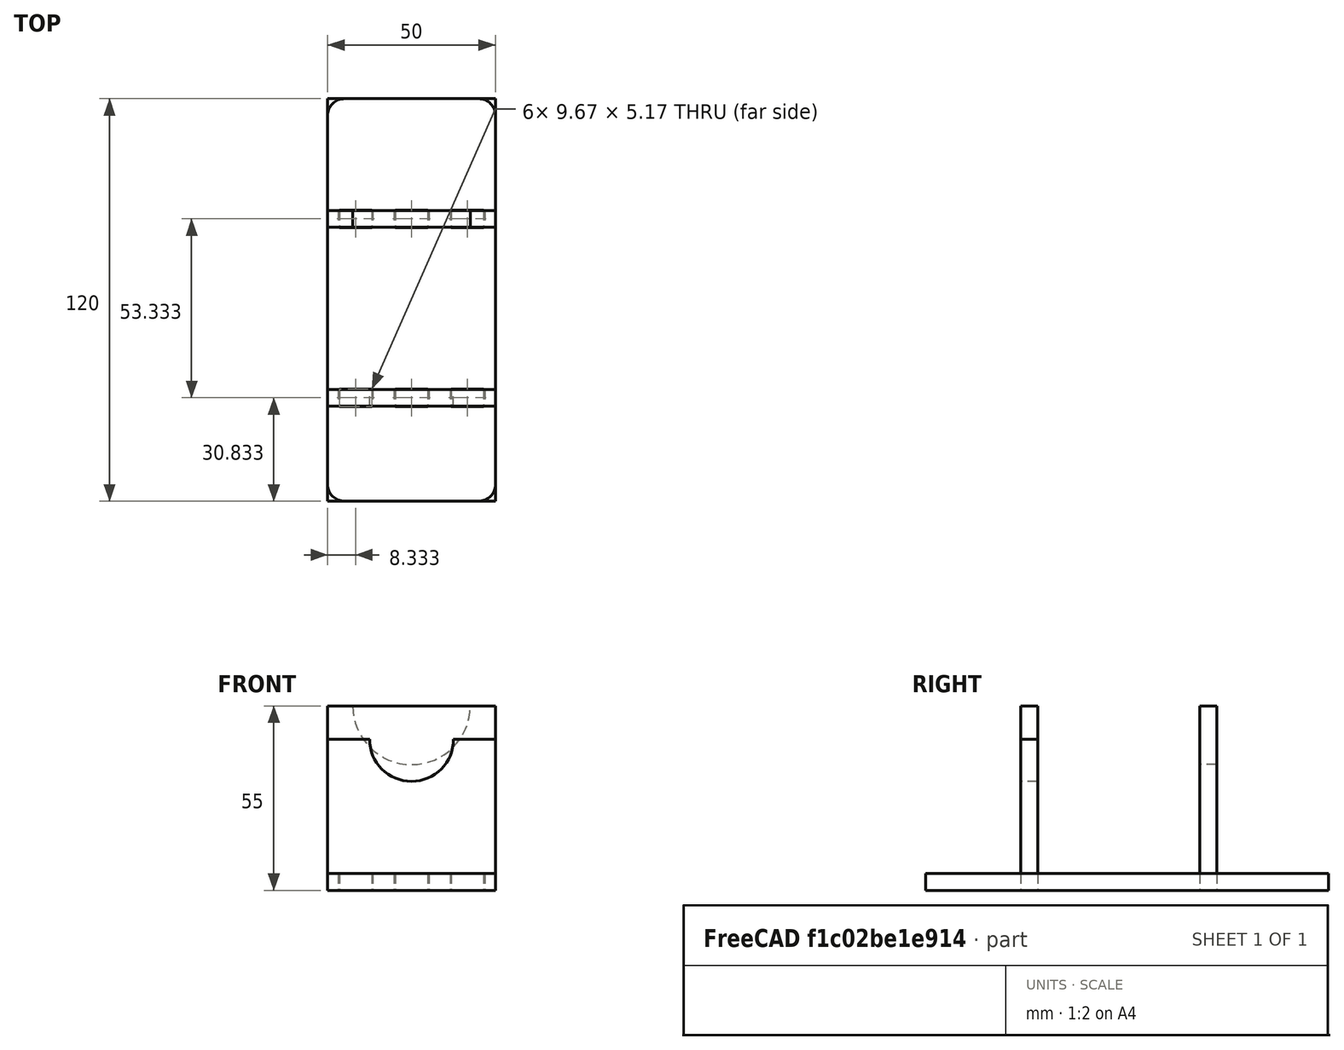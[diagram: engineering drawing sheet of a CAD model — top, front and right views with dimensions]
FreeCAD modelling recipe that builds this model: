
FCSTD DOCUMENT  (FreeCAD 0.19R24276 (Git))
Label: soldering_iron_stand
License: All rights reserved
LicenseURL: http://en.wikipedia.org/wiki/All_rights_reserved
objects: TechDraw::DrawProjGroupItem×27, TechDraw::DrawViewDimension×14, Part::Feature×6, PartDesign::FeatureBase×3, PartDesign::Body×3, TechDraw::DrawSVGTemplate×3, TechDraw::DrawProjGroup×3, TechDraw::DrawPage×3, Part::FeaturePython×2, Sketcher::SketchObject×2, PartDesign::Pocket×2, Spreadsheet::Sheet×1, App::DocumentObjectGroup×1, PartDesign::Fillet×1
note: 22 computed .brp shape members not serialized (recipe doc carries the construction recipe); baked Part::Feature solids carry a one-line shape summary decoded from their .brp

FEATURE [Spreadsheet::Sheet] Spreadsheet  label="parameters"
  cells = A1=width; B1(width)=120; A2=height; B2(height)=60; A3=depth; B3(depth)=50; A4=thickness; B4(thickness)=5
FEATURE [Part::Feature] face_panel
  Placement = pos=(0,-33.3333,0) rot=(0,0,1;0rad)
  shape: bbox 50 x 5 x 50 mm, 6 faces (baked)
  expr: .Placement.Base.y = <<parameters>>.depth / 1.5 * -1
FEATURE [Part::Feature] behind_panel
  Placement = pos=(0,-86.6667,0) rot=(0,0,1;0rad)
  shape: bbox 50 x 5 x 50 mm, 6 faces (baked)
  expr: .Placement.Base.y = (<<parameters>>.width - <<parameters>>.depth / 1.5) * -1
FEATURE [Part::Feature] bottom_panel
  shape: bbox 50 x 120 x 5 mm, 6 faces (baked)
FEATURE [Part::FeaturePython] Box  # WARN: FeaturePython — macro-defined, semantics opaque (R4)
  parts = -> [face_panel,behind_panel,bottom_panel]
FEATURE [App::DocumentObjectGroup] MultiJoin_origin_parts
  Group = -> [face_panel,behind_panel,bottom_panel]
FEATURE [Part::Feature] face_panel_tab
  shape: bbox 50 x 5 x 55 mm, 24 faces (baked)
FEATURE [Part::Feature] behind_panel_tab
  shape: bbox 50 x 5 x 55 mm, 24 faces (baked)
FEATURE [Part::Feature] bottom_panel_tab
  shape: bbox 50 x 120 x 5 mm, 30 faces (baked)
FEATURE [Part::FeaturePython] MultiJoin  # WARN: FeaturePython — macro-defined, semantics opaque (R4)
  fromParts = -> [MultiJoin_origin_parts,face_panel,behind_panel,bottom_panel]
  generatedParts = -> [face_panel_tab,behind_panel_tab,bottom_panel_tab]
FEATURE [PartDesign::FeatureBase] BaseFeature
  BaseFeature = -> face_panel_tab
FEATURE [Sketcher::SketchObject] Sketch
  ExternalGeometry = -> [BaseFeature]
  FullyConstrained = true
  MapMode = 5
  Placement = pos=(0,0,0) rot=(1,0,0;1.5708rad)
  Support = -> [XZ_Plane]
  expr: Constraints[1] = 35 / 2
  sketch-geometry (1):
    g0: Circle CenterX=0 CenterY=25 CenterZ=0 NormalX=0 NormalY=0 NormalZ=1 AngleXU=0 Radius=17.5
  constraints (3):
    c: PointOnObject(g0,g-3)
    c: Radius(g0) = 17.5
    c: PointOnObject(g0,g-2)
FEATURE [PartDesign::Pocket] Pocket
  BaseFeature = -> BaseFeature
  Length = 23
  Length2 = 100
  Profile = -> Sketch
  Type = 1
FEATURE [PartDesign::Body] Body  label="big_support001"
  BaseFeature = -> face_panel_tab
  Group = -> [BaseFeature,Sketch,Pocket]
  Origin = -> Origin
  Tip = -> Pocket
FEATURE [PartDesign::FeatureBase] BaseFeature001
  BaseFeature = -> behind_panel_tab
FEATURE [Sketcher::SketchObject] Sketch001
  ExternalGeometry = -> [BaseFeature001]
  FullyConstrained = true
  MapMode = 5
  Placement = pos=(0,-31.6667,0) rot=(1,0,0;1.5708rad)
  Support = -> [BaseFeature001]
  expr: Constraints[9] = <<parameters>>.thickness * 2
  expr: Constraints[14] = 25 / 2
  sketch-geometry (7):
    g0: LineSegment StartX=-25 StartY=25 StartZ=0 EndX=25 EndY=25 EndZ=0
    g1: LineSegment StartX=25 StartY=25 StartZ=0 EndX=25 EndY=15 EndZ=0
    g2: LineSegment StartX=25 StartY=15 StartZ=0 EndX=-25 EndY=15 EndZ=0
    g3: LineSegment StartX=-25 StartY=15 StartZ=0 EndX=-25 EndY=25 EndZ=0
    g4: ArcOfCircle CenterX=0 CenterY=15 CenterZ=0 NormalX=0 NormalY=0 NormalZ=1 AngleXU=0 Radius=12.5 StartAngle=3.14159 EndAngle=6.28319
    g5: LineSegment StartX=-25 StartY=15 StartZ=0 EndX=-12.5 EndY=15 EndZ=0
    g6: LineSegment StartX=25 StartY=15 StartZ=0 EndX=12.5 EndY=15 EndZ=0
  constraints (20):
    c: Coincident(g0,g1)
    c: Coincident(g1,g2)
    c: Coincident(g2,g3)
    c: Coincident(g3,g0)
    c: Horizontal(g0)
    c: Vertical(g1)
    c: Vertical(g3)
    c: Coincident(g0,g-3)
    c: PointOnObject(g1,g-4)
    c: DistanceY(g1,g1) = 10
    c: PointOnObject(g4,g-2)
    c: PointOnObject(g4,g2)
    c: PointOnObject(g4,g2)
    c: PointOnObject(g4,g2)
    c: Radius(g4) = 12.5
    c: Coincident(g5,g2)
    c: Coincident(g5,g4)
    c: Horizontal(g5)
    c: Coincident(g6,g1)
    c: Coincident(g6,g4)
FEATURE [PartDesign::Pocket] Pocket001
  BaseFeature = -> BaseFeature001
  Length = 5
  Length2 = 100
  Profile = -> Sketch001
  Type = 0
FEATURE [PartDesign::Body] Body001  label="small_support001"
  BaseFeature = -> behind_panel_tab
  Group = -> [BaseFeature001,Sketch001,Pocket001]
  Origin = -> Origin001
  Tip = -> Pocket001
FEATURE [PartDesign::FeatureBase] BaseFeature002
  BaseFeature = -> bottom_panel_tab
FEATURE [PartDesign::Fillet] Fillet
  Base = -> BaseFeature002 [Edge1,Edge5,Edge8,Edge2]
  BaseFeature = -> BaseFeature002
  Radius = 5
  SupportTransform = false
FEATURE [PartDesign::Body] Body002  label="base001"
  BaseFeature = -> bottom_panel_tab
  Group = -> [BaseFeature002,Fillet]
  Origin = -> Origin002
  Tip = -> Fillet
FEATURE [TechDraw::DrawSVGTemplate] Template_Pocket
  Height = 210
  Orientation = 1
  Width = 297
FEATURE [TechDraw::DrawProjGroupItem] ProjItem  label="Front"
  CoarseView = false
  Direction = (0,-1,0)
  Focus = 100
  HardHidden = false
  IsoCount = 0
  IsoHidden = false
  IsoVisible = false
  LockPosition = true
  Perspective = false
  Rotation = 0
  RotationVector = (1,0,0)
  Scale = 0.5
  ScaleType = 2
  SeamHidden = false
  SeamVisible = true
  SmoothHidden = false
  SmoothVisible = true
  Source = -> [Pocket]
  Type = 0
  X = 0
  XDirection = (1,0,0)
  Y = 0
FEATURE [TechDraw::DrawProjGroupItem] ProjItem001  label="Right"
  CoarseView = false
  Direction = (1,-1e-16,0)
  Focus = 100
  HardHidden = false
  IsoCount = 0
  IsoHidden = false
  IsoVisible = false
  LockPosition = false
  Perspective = false
  Rotation = 0
  RotationVector = (1,0,0)
  Scale = 0.5
  ScaleType = 2
  SeamHidden = false
  SeamVisible = true
  SmoothHidden = false
  SmoothVisible = true
  Source = -> [Pocket]
  Type = 2
  X = -32.767
  XDirection = (1e-16,1,0)
  Y = 0
FEATURE [TechDraw::DrawProjGroupItem] ProjItem002  label="Top"
  CoarseView = false
  Direction = (0,0,1)
  Focus = 100
  HardHidden = false
  IsoCount = 0
  IsoHidden = false
  IsoVisible = false
  LockPosition = false
  Perspective = false
  Rotation = 0
  RotationVector = (1,0,0)
  Scale = 0.5
  ScaleType = 2
  SeamHidden = false
  SeamVisible = true
  SmoothHidden = false
  SmoothVisible = true
  Source = -> [Pocket]
  Type = 4
  X = 0
  XDirection = (1,0,0)
  Y = -63.3011
FEATURE [TechDraw::DrawProjGroupItem] ProjItem003  label="Left"
  CoarseView = false
  Direction = (-1,-1e-16,0)
  Focus = 100
  HardHidden = false
  IsoCount = 0
  IsoHidden = false
  IsoVisible = false
  LockPosition = false
  Perspective = false
  Rotation = 0
  RotationVector = (1,0,0)
  Scale = 0.5
  ScaleType = 2
  SeamHidden = false
  SeamVisible = true
  SmoothHidden = false
  SmoothVisible = true
  Source = -> [Pocket]
  Type = 1
  X = 32.767
  XDirection = (1e-16,-1,0)
  Y = 0
FEATURE [TechDraw::DrawProjGroupItem] ProjItem004  label="Bottom"
  CoarseView = false
  Direction = (0,0,-1)
  Focus = 100
  HardHidden = false
  IsoCount = 0
  IsoHidden = false
  IsoVisible = false
  LockPosition = false
  Perspective = false
  Rotation = 0
  RotationVector = (1,0,0)
  Scale = 0.5
  ScaleType = 2
  SeamHidden = false
  SeamVisible = true
  SmoothHidden = false
  SmoothVisible = true
  Source = -> [Pocket]
  Type = 5
  X = 0
  XDirection = (1,0,0)
  Y = 32.767
FEATURE [TechDraw::DrawProjGroupItem] ProjItem005  label="FrontBottomLeft"
  CoarseView = false
  Direction = (-0.57735,-0.57735,-0.57735)
  Focus = 100
  HardHidden = false
  IsoCount = 0
  IsoHidden = false
  IsoVisible = false
  LockPosition = false
  Perspective = false
  Rotation = 0
  RotationVector = (1,0,0)
  Scale = 0.5
  ScaleType = 2
  SeamHidden = false
  SeamVisible = true
  SmoothHidden = false
  SmoothVisible = true
  Source = -> [Pocket]
  Type = 8
  X = 41.2398
  XDirection = (0.707107,-0.707107,0)
  Y = 48.0341
FEATURE [TechDraw::DrawProjGroupItem] ProjItem006  label="FrontTopRight"
  CoarseView = false
  Direction = (0.57735,-0.57735,0.57735)
  Focus = 100
  HardHidden = false
  IsoCount = 0
  IsoHidden = false
  IsoVisible = false
  LockPosition = false
  Perspective = false
  Rotation = 0
  RotationVector = (1,0,0)
  Scale = 0.5
  ScaleType = 2
  SeamHidden = false
  SeamVisible = true
  SmoothHidden = false
  SmoothVisible = true
  Source = -> [Pocket]
  Type = 7
  X = -41.2398
  XDirection = (0.707107,0.707107,0)
  Y = -48.0341
FEATURE [TechDraw::DrawProjGroupItem] ProjItem007  label="FrontTopLeft"
  CoarseView = false
  Direction = (-0.57735,-0.57735,0.57735)
  Focus = 100
  HardHidden = false
  IsoCount = 0
  IsoHidden = false
  IsoVisible = false
  LockPosition = false
  Perspective = false
  Rotation = 0
  RotationVector = (1,0,0)
  Scale = 0.5
  ScaleType = 2
  SeamHidden = false
  SeamVisible = true
  SmoothHidden = false
  SmoothVisible = true
  Source = -> [Pocket]
  Type = 6
  X = 41.2398
  XDirection = (0.707107,-0.707107,0)
  Y = -48.0341
FEATURE [TechDraw::DrawProjGroupItem] ProjItem008  label="FrontBottomRight"
  CoarseView = false
  Direction = (0.57735,-0.57735,-0.57735)
  Focus = 100
  HardHidden = false
  IsoCount = 0
  IsoHidden = false
  IsoVisible = false
  LockPosition = false
  Perspective = false
  Rotation = 0
  RotationVector = (1,0,0)
  Scale = 0.5
  ScaleType = 2
  SeamHidden = false
  SeamVisible = true
  SmoothHidden = false
  SmoothVisible = true
  Source = -> [Pocket]
  Type = 9
  X = -41.2398
  XDirection = (0.707107,0.707107,0)
  Y = 48.0341
FEATURE [TechDraw::DrawProjGroup] ProjGroup_Pocket
  Anchor = -> ProjItem
  AutoDistribute = true
  LockPosition = false
  ProjectionType = 0
  Rotation = 0
  Scale = 0.5
  ScaleType = 1
  Source = -> [Pocket]
  Views = -> [ProjItem,ProjItem001,ProjItem002,ProjItem003,ProjItem004,ProjItem005,ProjItem006,ProjItem007,ProjItem008]
  X = 148.5
  Y = 105
  spacingX = 15
  spacingY = 15
FEATURE [TechDraw::DrawSVGTemplate] Template_Pocket001
  Height = 210
  Orientation = 1
  Width = 297
FEATURE [TechDraw::DrawProjGroupItem] ProjItem009  label="Front001"
  CoarseView = false
  Direction = (0,-1,0)
  Focus = 100
  HardHidden = false
  IsoCount = 0
  IsoHidden = false
  IsoVisible = false
  LockPosition = true
  Perspective = false
  Rotation = 0
  RotationVector = (1,0,0)
  Scale = 0.75
  ScaleType = 2
  SeamHidden = false
  SeamVisible = true
  SmoothHidden = false
  SmoothVisible = true
  Source = -> [Pocket001]
  Type = 0
  X = 0
  XDirection = (1,0,0)
  Y = 0
FEATURE [TechDraw::DrawProjGroupItem] ProjItem010  label="Right001"
  CoarseView = false
  Direction = (1,-1e-16,0)
  Focus = 100
  HardHidden = false
  IsoCount = 0
  IsoHidden = false
  IsoVisible = false
  LockPosition = false
  Perspective = false
  Rotation = 0
  RotationVector = (1,0,0)
  Scale = 0.75
  ScaleType = 2
  SeamHidden = false
  SeamVisible = true
  SmoothHidden = false
  SmoothVisible = true
  Source = -> [Pocket001]
  Type = 2
  X = -38.5887
  XDirection = (1e-16,1,0)
  Y = 0
FEATURE [TechDraw::DrawProjGroupItem] ProjItem011  label="Top001"
  CoarseView = false
  Direction = (0,0,1)
  Focus = 100
  HardHidden = false
  IsoCount = 0
  IsoHidden = false
  IsoVisible = false
  LockPosition = false
  Perspective = false
  Rotation = 0
  RotationVector = (1,0,0)
  Scale = 0.75
  ScaleType = 2
  SeamHidden = false
  SeamVisible = true
  SmoothHidden = false
  SmoothVisible = true
  Source = -> [Pocket001]
  Type = 4
  X = 0
  XDirection = (1,0,0)
  Y = -78.2661
FEATURE [TechDraw::DrawProjGroupItem] ProjItem012  label="Left001"
  CoarseView = false
  Direction = (-1,-1e-16,0)
  Focus = 100
  HardHidden = false
  IsoCount = 0
  IsoHidden = false
  IsoVisible = false
  LockPosition = false
  Perspective = false
  Rotation = 0
  RotationVector = (1,0,0)
  Scale = 0.75
  ScaleType = 2
  SeamHidden = false
  SeamVisible = true
  SmoothHidden = false
  SmoothVisible = true
  Source = -> [Pocket001]
  Type = 1
  X = 38.5887
  XDirection = (1e-16,-1,0)
  Y = 0
FEATURE [TechDraw::DrawProjGroupItem] ProjItem013  label="Bottom001"
  CoarseView = false
  Direction = (0,0,-1)
  Focus = 100
  HardHidden = false
  IsoCount = 0
  IsoHidden = false
  IsoVisible = false
  LockPosition = false
  Perspective = false
  Rotation = 0
  RotationVector = (1,0,0)
  Scale = 0.75
  ScaleType = 2
  SeamHidden = false
  SeamVisible = true
  SmoothHidden = false
  SmoothVisible = true
  Source = -> [Pocket001]
  Type = 5
  X = 0
  XDirection = (1,0,0)
  Y = 38.5887
FEATURE [TechDraw::DrawProjGroupItem] ProjItem014  label="FrontBottomLeft001"
  CoarseView = false
  Direction = (-0.57735,-0.57735,-0.57735)
  Focus = 100
  HardHidden = false
  IsoCount = 0
  IsoHidden = false
  IsoVisible = false
  LockPosition = false
  Perspective = false
  Rotation = 0
  RotationVector = (1,0,0)
  Scale = 0.75
  ScaleType = 2
  SeamHidden = false
  SeamVisible = true
  SmoothHidden = false
  SmoothVisible = true
  Source = -> [Pocket001]
  Type = 8
  X = 51.2978
  XDirection = (0.707107,-0.707107,0)
  Y = 58.4274
FEATURE [TechDraw::DrawProjGroupItem] ProjItem015  label="FrontTopRight001"
  CoarseView = false
  Direction = (0.57735,-0.57735,0.57735)
  Focus = 100
  HardHidden = false
  IsoCount = 0
  IsoHidden = false
  IsoVisible = false
  LockPosition = false
  Perspective = false
  Rotation = 0
  RotationVector = (1,0,0)
  Scale = 0.75
  ScaleType = 2
  SeamHidden = false
  SeamVisible = true
  SmoothHidden = false
  SmoothVisible = true
  Source = -> [Pocket001]
  Type = 7
  X = -51.2978
  XDirection = (0.707107,0.707107,0)
  Y = -58.4274
FEATURE [TechDraw::DrawProjGroupItem] ProjItem016  label="FrontTopLeft001"
  CoarseView = false
  Direction = (-0.57735,-0.57735,0.57735)
  Focus = 100
  HardHidden = false
  IsoCount = 0
  IsoHidden = false
  IsoVisible = false
  LockPosition = false
  Perspective = false
  Rotation = 0
  RotationVector = (1,0,0)
  Scale = 0.75
  ScaleType = 2
  SeamHidden = false
  SeamVisible = true
  SmoothHidden = false
  SmoothVisible = true
  Source = -> [Pocket001]
  Type = 6
  X = 51.2978
  XDirection = (0.707107,-0.707107,0)
  Y = -58.4274
FEATURE [TechDraw::DrawProjGroupItem] ProjItem017  label="FrontBottomRight001"
  CoarseView = false
  Direction = (0.57735,-0.57735,-0.57735)
  Focus = 100
  HardHidden = false
  IsoCount = 0
  IsoHidden = false
  IsoVisible = false
  LockPosition = false
  Perspective = false
  Rotation = 0
  RotationVector = (1,0,0)
  Scale = 0.75
  ScaleType = 2
  SeamHidden = false
  SeamVisible = true
  SmoothHidden = false
  SmoothVisible = true
  Source = -> [Pocket001]
  Type = 9
  X = -51.2978
  XDirection = (0.707107,0.707107,0)
  Y = 58.4274
FEATURE [TechDraw::DrawProjGroup] ProjGroup_Pocket001
  Anchor = -> ProjItem009
  AutoDistribute = true
  LockPosition = false
  ProjectionType = 0
  Rotation = 0
  Scale = 0.75
  ScaleType = 1
  Source = -> [Pocket001]
  Views = -> [ProjItem009,ProjItem010,ProjItem011,ProjItem012,ProjItem013,ProjItem014,ProjItem015,ProjItem016,ProjItem017]
  X = 148.5
  Y = 105
  spacingX = 15
  spacingY = 15
FEATURE [TechDraw::DrawSVGTemplate] Template_Fillet
  Height = 210
  Orientation = 1
  Width = 297
FEATURE [TechDraw::DrawProjGroupItem] ProjItem018  label="Front002"
  CoarseView = false
  Direction = (0,-1,0)
  Focus = 100
  HardHidden = false
  IsoCount = 0
  IsoHidden = false
  IsoVisible = false
  LockPosition = true
  Perspective = false
  Rotation = 0
  RotationVector = (1,0,0)
  Scale = 0.5
  ScaleType = 2
  SeamHidden = false
  SeamVisible = true
  SmoothHidden = false
  SmoothVisible = true
  Source = -> [Fillet]
  Type = 0
  X = 0
  XDirection = (1,0,0)
  Y = 0
FEATURE [TechDraw::DrawProjGroupItem] ProjItem019  label="Right002"
  CoarseView = false
  Direction = (1,-1e-16,0)
  Focus = 100
  HardHidden = false
  IsoCount = 0
  IsoHidden = false
  IsoVisible = false
  LockPosition = false
  Perspective = false
  Rotation = 0
  RotationVector = (1,0,0)
  Scale = 0.5
  ScaleType = 2
  SeamHidden = false
  SeamVisible = true
  SmoothHidden = false
  SmoothVisible = true
  Source = -> [Fillet]
  Type = 2
  X = -75
  XDirection = (1e-16,1,0)
  Y = 0
FEATURE [TechDraw::DrawProjGroupItem] ProjItem020  label="Top002"
  CoarseView = false
  Direction = (0,0,1)
  Focus = 100
  HardHidden = false
  IsoCount = 0
  IsoHidden = false
  IsoVisible = false
  LockPosition = false
  Perspective = false
  Rotation = 0
  RotationVector = (1,0,0)
  Scale = 0.5
  ScaleType = 2
  SeamHidden = false
  SeamVisible = true
  SmoothHidden = false
  SmoothVisible = true
  Source = -> [Fillet]
  Type = 4
  X = 0
  XDirection = (1,0,0)
  Y = -80
FEATURE [TechDraw::DrawProjGroupItem] ProjItem021  label="Left002"
  CoarseView = false
  Direction = (-1,-1e-16,0)
  Focus = 100
  HardHidden = false
  IsoCount = 0
  IsoHidden = false
  IsoVisible = false
  LockPosition = false
  Perspective = false
  Rotation = 0
  RotationVector = (1,0,0)
  Scale = 0.5
  ScaleType = 2
  SeamHidden = false
  SeamVisible = true
  SmoothHidden = false
  SmoothVisible = true
  Source = -> [Fillet]
  Type = 1
  X = 75
  XDirection = (1e-16,-1,0)
  Y = 0
FEATURE [TechDraw::DrawProjGroupItem] ProjItem022  label="Bottom002"
  CoarseView = false
  Direction = (0,0,-1)
  Focus = 100
  HardHidden = false
  IsoCount = 0
  IsoHidden = false
  IsoVisible = false
  LockPosition = false
  Perspective = false
  Rotation = 0
  RotationVector = (1,0,0)
  Scale = 0.5
  ScaleType = 2
  SeamHidden = false
  SeamVisible = true
  SmoothHidden = false
  SmoothVisible = true
  Source = -> [Fillet]
  Type = 5
  X = 0
  XDirection = (1,0,0)
  Y = 67.6743
FEATURE [TechDraw::DrawProjGroupItem] ProjItem023  label="FrontBottomLeft002"
  CoarseView = false
  Direction = (-0.57735,-0.57735,-0.57735)
  Focus = 100
  HardHidden = false
  IsoCount = 0
  IsoHidden = false
  IsoVisible = false
  LockPosition = false
  Perspective = false
  Rotation = 0
  RotationVector = (1,0,0)
  Scale = 0.5
  ScaleType = 2
  SeamHidden = false
  SeamVisible = true
  SmoothHidden = false
  SmoothVisible = true
  Source = -> [Fillet]
  Type = 8
  X = 76.1261
  XDirection = (0.707107,-0.707107,0)
  Y = 41.7554
FEATURE [TechDraw::DrawProjGroupItem] ProjItem024  label="FrontTopRight002"
  CoarseView = false
  Direction = (0.57735,-0.57735,0.57735)
  Focus = 100
  HardHidden = false
  IsoCount = 0
  IsoHidden = false
  IsoVisible = false
  LockPosition = false
  Perspective = false
  Rotation = 0
  RotationVector = (1,0,0)
  Scale = 0.5
  ScaleType = 2
  SeamHidden = false
  SeamVisible = true
  SmoothHidden = false
  SmoothVisible = true
  Source = -> [Fillet]
  Type = 7
  X = -73.6649
  XDirection = (0.707107,0.707107,0)
  Y = -65.5056
FEATURE [TechDraw::DrawProjGroupItem] ProjItem025  label="FrontTopLeft002"
  CoarseView = false
  Direction = (-0.57735,-0.57735,0.57735)
  Focus = 100
  HardHidden = false
  IsoCount = 0
  IsoHidden = false
  IsoVisible = false
  LockPosition = false
  Perspective = false
  Rotation = 0
  RotationVector = (1,0,0)
  Scale = 0.5
  ScaleType = 2
  SeamHidden = false
  SeamVisible = true
  SmoothHidden = false
  SmoothVisible = true
  Source = -> [Fillet]
  Type = 6
  X = 74.0165
  XDirection = (0.707107,-0.707107,0)
  Y = -92.2267
FEATURE [TechDraw::DrawProjGroupItem] ProjItem026  label="FrontBottomRight002"
  CoarseView = false
  Direction = (0.57735,-0.57735,-0.57735)
  Focus = 100
  HardHidden = false
  IsoCount = 0
  IsoHidden = false
  IsoVisible = false
  LockPosition = false
  Perspective = false
  Rotation = 0
  RotationVector = (1,0,0)
  Scale = 0.5
  ScaleType = 2
  SeamHidden = false
  SeamVisible = true
  SmoothHidden = false
  SmoothVisible = true
  Source = -> [Fillet]
  Type = 9
  X = -72.6101
  XDirection = (0.707107,0.707107,0)
  Y = 55.8191
FEATURE [TechDraw::DrawProjGroup] ProjGroup_Fillet
  Anchor = -> ProjItem018
  AutoDistribute = true
  LockPosition = false
  ProjectionType = 0
  Rotation = 0
  Scale = 0.5
  ScaleType = 1
  Source = -> [Fillet]
  Views = -> [ProjItem018,ProjItem019,ProjItem020,ProjItem021,ProjItem022,ProjItem023,ProjItem024,ProjItem025,ProjItem026]
  X = 148.5
  Y = 105
  spacingX = 15
  spacingY = 15
FEATURE [TechDraw::DrawViewDimension] Dimension
  Arbitrary = false
  ArbitraryTolerances = false
  EqualTolerance = true
  FormatSpec = %.2f
  FormatSpecOverTolerance = %+.2f
  FormatSpecUnderTolerance = %+.2f
  Inverted = false
  LockPosition = false
  MeasureType = 1
  OverTolerance = 0
  References2D = -> [ProjItem022]
  Rotation = 0
  ScaleType = 0
  TheoreticalExact = false
  Type = 2
  UnderTolerance = 0
  X = 24.0637
  Y = -3.51593
FEATURE [TechDraw::DrawViewDimension] Dimension001
  Arbitrary = false
  ArbitraryTolerances = false
  EqualTolerance = true
  FormatSpec = %.2f
  FormatSpecOverTolerance = %+.2f
  FormatSpecUnderTolerance = %+.2f
  Inverted = false
  LockPosition = false
  MeasureType = 1
  OverTolerance = 0
  References2D = -> [ProjItem022]
  Rotation = 0
  ScaleType = 0
  TheoreticalExact = false
  Type = 1
  UnderTolerance = 0
  X = 0.703187
  Y = -43.6733
FEATURE [TechDraw::DrawViewDimension] Dimension002
  Arbitrary = false
  ArbitraryTolerances = false
  EqualTolerance = true
  FormatSpec = %.2f
  FormatSpecOverTolerance = %+.2f
  FormatSpecUnderTolerance = %+.2f
  Inverted = false
  LockPosition = false
  MeasureType = 1
  OverTolerance = 0
  References2D = -> [ProjItem022]
  Rotation = 0
  ScaleType = 0
  TheoreticalExact = false
  Type = 2
  UnderTolerance = 0
  X = -30.81
  Y = 1.62148
FEATURE [TechDraw::DrawViewDimension] Dimension003
  Arbitrary = false
  ArbitraryTolerances = false
  EqualTolerance = true
  FormatSpec = %.2f
  FormatSpecOverTolerance = %+.2f
  FormatSpecUnderTolerance = %+.2f
  Inverted = false
  LockPosition = false
  MeasureType = 1
  OverTolerance = 0
  References2D = -> [ProjItem022]
  Rotation = 0
  ScaleType = 0
  TheoreticalExact = false
  Type = 2
  UnderTolerance = 0
  X = -22.6374
  Y = 0.692779
FEATURE [TechDraw::DrawViewDimension] Dimension004
  Arbitrary = false
  ArbitraryTolerances = false
  EqualTolerance = true
  FormatSpec = %.2f
  FormatSpecOverTolerance = %+.2f
  FormatSpecUnderTolerance = %+.2f
  Inverted = false
  LockPosition = false
  MeasureType = 1
  OverTolerance = 0
  References2D = -> [ProjItem022]
  Rotation = 0
  ScaleType = 0
  TheoreticalExact = false
  Type = 2
  UnderTolerance = 0
  X = 17.6224
  Y = 6.41076
FEATURE [TechDraw::DrawViewDimension] Dimension005
  Arbitrary = false
  ArbitraryTolerances = false
  EqualTolerance = true
  FormatSpec = %.2f
  FormatSpecOverTolerance = %+.2f
  FormatSpecUnderTolerance = %+.2f
  Inverted = false
  LockPosition = false
  MeasureType = 1
  OverTolerance = 0
  References2D = -> [ProjItem022]
  Rotation = 0
  ScaleType = 0
  TheoreticalExact = false
  Type = 1
  UnderTolerance = 0
  X = -1.48592
  Y = 4.81053
FEATURE [TechDraw::DrawViewDimension] Dimension006
  Arbitrary = false
  ArbitraryTolerances = false
  EqualTolerance = true
  FormatSpec = %.2f
  FormatSpecOverTolerance = %+.2f
  FormatSpecUnderTolerance = %+.2f
  Inverted = false
  LockPosition = false
  MeasureType = 1
  OverTolerance = 0
  References2D = -> [ProjItem018]
  Rotation = 0
  ScaleType = 0
  TheoreticalExact = false
  Type = 2
  UnderTolerance = 0
  X = 23.1821
  Y = 7.29095
FEATURE [TechDraw::DrawPage] Page_Fillet  label="base"
  KeepUpdated = true
  NextBalloonIndex = 1
  ProjectionType = 0
  Template = -> Template_Fillet
  Views = -> [ProjGroup_Fillet,Dimension,Dimension001,Dimension002,Dimension003,Dimension004,Dimension005,Dimension006]
FEATURE [TechDraw::DrawViewDimension] Dimension007
  Arbitrary = false
  ArbitraryTolerances = false
  EqualTolerance = true
  FormatSpec = %.2f
  FormatSpecOverTolerance = %+.2f
  FormatSpecUnderTolerance = %+.2f
  Inverted = false
  LockPosition = false
  MeasureType = 1
  OverTolerance = 0
  References2D = -> [ProjItem009]
  Rotation = 0
  ScaleType = 0
  TheoreticalExact = false
  Type = 2
  UnderTolerance = 0
  X = 21.0678
  Y = -32.1851
FEATURE [TechDraw::DrawViewDimension] Dimension008
  Arbitrary = false
  ArbitraryTolerances = false
  EqualTolerance = true
  FormatSpec = %.2f
  FormatSpecOverTolerance = %+.2f
  FormatSpecUnderTolerance = %+.2f
  Inverted = false
  LockPosition = false
  MeasureType = 1
  OverTolerance = 0
  References2D = -> [ProjItem009]
  Rotation = 0
  ScaleType = 0
  TheoreticalExact = false
  Type = 1
  UnderTolerance = 0
  X = 0.318665
  Y = 28.9843
FEATURE [TechDraw::DrawViewDimension] Dimension009
  Arbitrary = false
  ArbitraryTolerances = false
  EqualTolerance = true
  FormatSpec = %.2f
  FormatSpecOverTolerance = %+.2f
  FormatSpecUnderTolerance = %+.2f
  Inverted = false
  LockPosition = false
  MeasureType = 1
  OverTolerance = 0
  References2D = -> [ProjItem009]
  Rotation = 0
  ScaleType = 0
  TheoreticalExact = false
  Type = 1
  UnderTolerance = 0
  X = -15.778
  Y = -30.5523
FEATURE [TechDraw::DrawViewDimension] Dimension010
  Arbitrary = false
  ArbitraryTolerances = false
  EqualTolerance = true
  FormatSpec = %.2f
  FormatSpecOverTolerance = %+.2f
  FormatSpecUnderTolerance = %+.2f
  Inverted = false
  LockPosition = false
  MeasureType = 1
  OverTolerance = 0
  References2D = -> [ProjItem009]
  Rotation = 0
  ScaleType = 0
  TheoreticalExact = false
  Type = 1
  UnderTolerance = 0
  X = 1.43525
  Y = -20.5632
FEATURE [TechDraw::DrawViewDimension] Dimension011
  Arbitrary = false
  ArbitraryTolerances = false
  EqualTolerance = true
  FormatSpec = %.2f
  FormatSpecOverTolerance = %+.2f
  FormatSpecUnderTolerance = %+.2f
  Inverted = false
  LockPosition = false
  MeasureType = 1
  OverTolerance = 0
  References2D = -> [ProjItem010]
  Rotation = 0
  ScaleType = 0
  TheoreticalExact = false
  Type = 1
  UnderTolerance = 0
  X = -26.2618
  Y = 25.1239
FEATURE [TechDraw::DrawPage] Page_Pocket001  label="small_support"
  KeepUpdated = true
  NextBalloonIndex = 1
  ProjectionType = 0
  Template = -> Template_Pocket001
  Views = -> [ProjGroup_Pocket001,Dimension007,Dimension008,Dimension009,Dimension010,Dimension011]
FEATURE [TechDraw::DrawViewDimension] Dimension012
  Arbitrary = false
  ArbitraryTolerances = false
  EqualTolerance = true
  FormatSpec = %.2f
  FormatSpecOverTolerance = %+.2f
  FormatSpecUnderTolerance = %+.2f
  Inverted = false
  LockPosition = false
  MeasureType = 1
  OverTolerance = 0
  References2D = -> [ProjItem]
  Rotation = 0
  ScaleType = 0
  TheoreticalExact = false
  Type = 2
  UnderTolerance = 0
  X = 17.7939
  Y = 1.10647
FEATURE [TechDraw::DrawViewDimension] Dimension013
  Arbitrary = false
  ArbitraryTolerances = false
  EqualTolerance = true
  FormatSpec = %.2f
  FormatSpecOverTolerance = %+.2f
  FormatSpecUnderTolerance = %+.2f
  Inverted = false
  LockPosition = false
  MeasureType = 1
  OverTolerance = 0
  References2D = -> [ProjItem]
  Rotation = 0
  ScaleType = 0
  TheoreticalExact = false
  Type = 1
  UnderTolerance = 0
  X = 0.368825
  Y = 24.9992
FEATURE [TechDraw::DrawPage] Page_Pocket  label="big_support"
  KeepUpdated = true
  NextBalloonIndex = 1
  ProjectionType = 0
  Template = -> Template_Pocket
  Views = -> [ProjGroup_Pocket,Dimension012,Dimension013]
